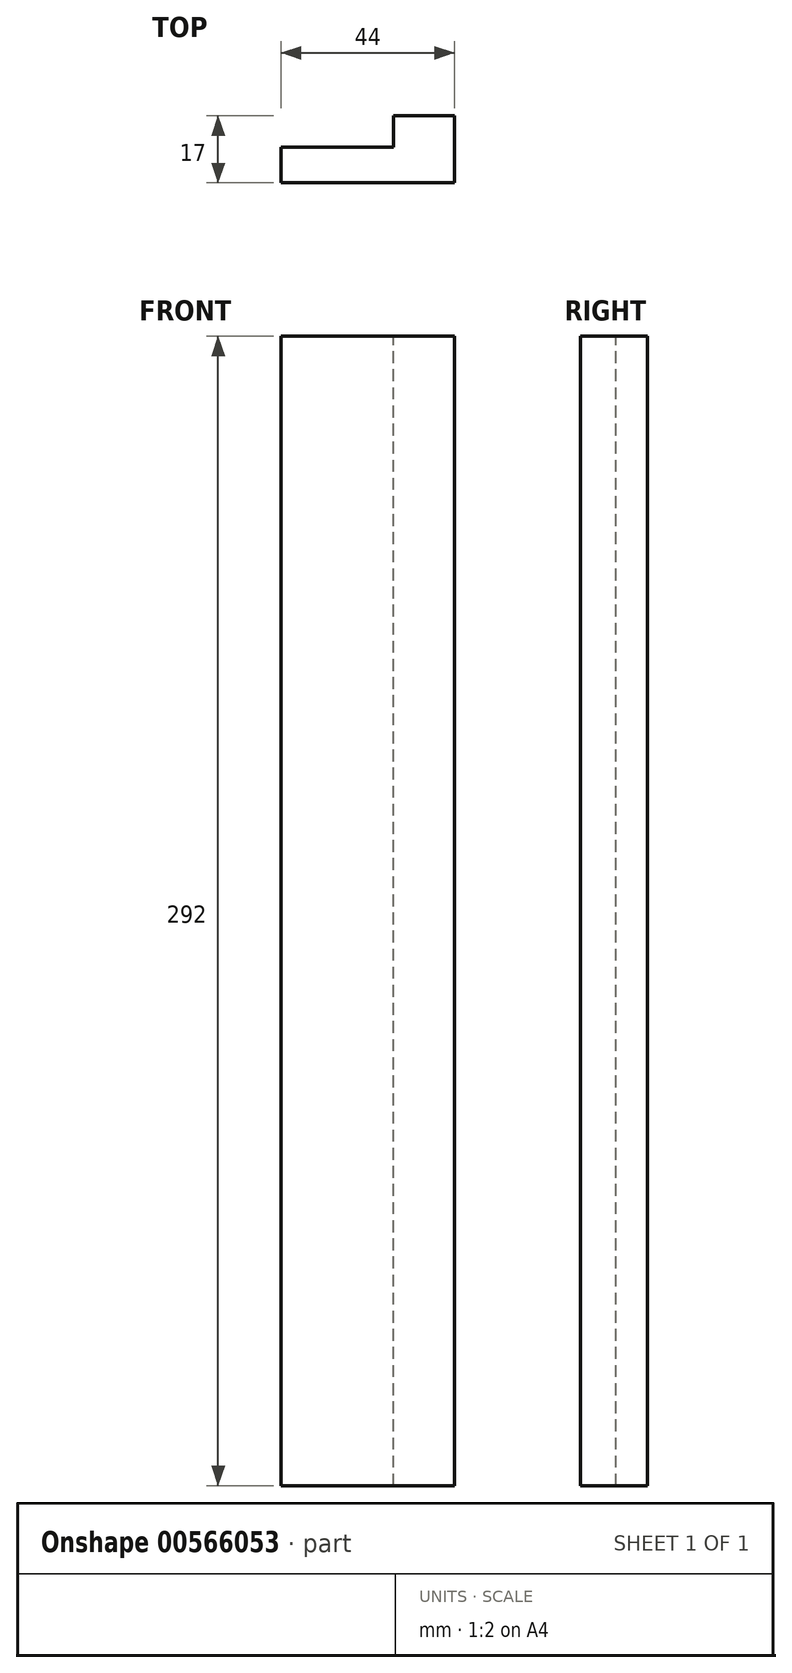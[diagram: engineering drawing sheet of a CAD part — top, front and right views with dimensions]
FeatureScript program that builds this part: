
annotation { "Feature Type Name" : "Feature", "Feature Type Description" : "" }
export const myFeature = defineFeature(function(context is Context, id is Id, definition is map)
    precondition{}
    {
        {
            var Q0;
            Q0=qCreatedBy(makeId("Front.planeOp"),FACE);
            var sketch = newSketch(context, id + "F0", { "sketchPlane" : qUnion([Q0])});
            skLineSegment(sketch, "E0.bottom", {"start": v(36.71, 217.99) * mm, "end": v(80.71, 217.99) * mm});
            skLineSegment(sketch, "E0.top", {"start": v(36.71, -74.01) * mm, "end": v(80.71, -74.01) * mm});
            skLineSegment(sketch, "E0.left", {"start": v(36.71, 217.99) * mm, "end": v(36.71, -74.01) * mm});
            skLineSegment(sketch, "E0.right", {"start": v(80.71, 217.99) * mm, "end": v(80.71, -74.01) * mm});
            skSolve(sketch);
        }
        {
            var Q0;
            Q0 = qSketchRegion(id + "F0", true);
            extrude(context, id + "F1", {"entities" : qUnion([Q0]), "depth" : 17 * mm, "offsetDistance" : 25 * mm});
        }
        {
            var Q0;
            Q0=makeQuery(id+"F1.opExtrude","SWEPT_FACE",FACE,{"disambiguationData":[OSD([sQuery(id+"F0.wireOp",EDGE,"E0.bottom")])]});
            var sketch = newSketch(context, id + "F2", { "sketchPlane" : qUnion([Q0])});
            skLineSegment(sketch, "E1.right", {"start": v(65.21, 0) * mm, "end": v(65.21, -8) * mm});
            skLineSegment(sketch, "E2.bottom", {"start": v(36.71, 0) * mm, "end": v(65.21, 0) * mm});
            skLineSegment(sketch, "E2.top", {"start": v(36.71, -8) * mm, "end": v(65.21, -8) * mm});
            skLineSegment(sketch, "E2.left", {"start": v(36.71, 0) * mm, "end": v(36.71, -8) * mm});
            skSolve(sketch);
        }
        {
            var Q0;
            Q0 = qSketchRegion(id + "F2", true);
            extrude(context, id + "F3", {"entities" : qUnion([Q0]), "operationType" : NewBodyOperationType.REMOVE, "oppositeDirection" : true, "depth" : 292 * mm, "offsetDistance" : 25 * mm});
        }
    });
